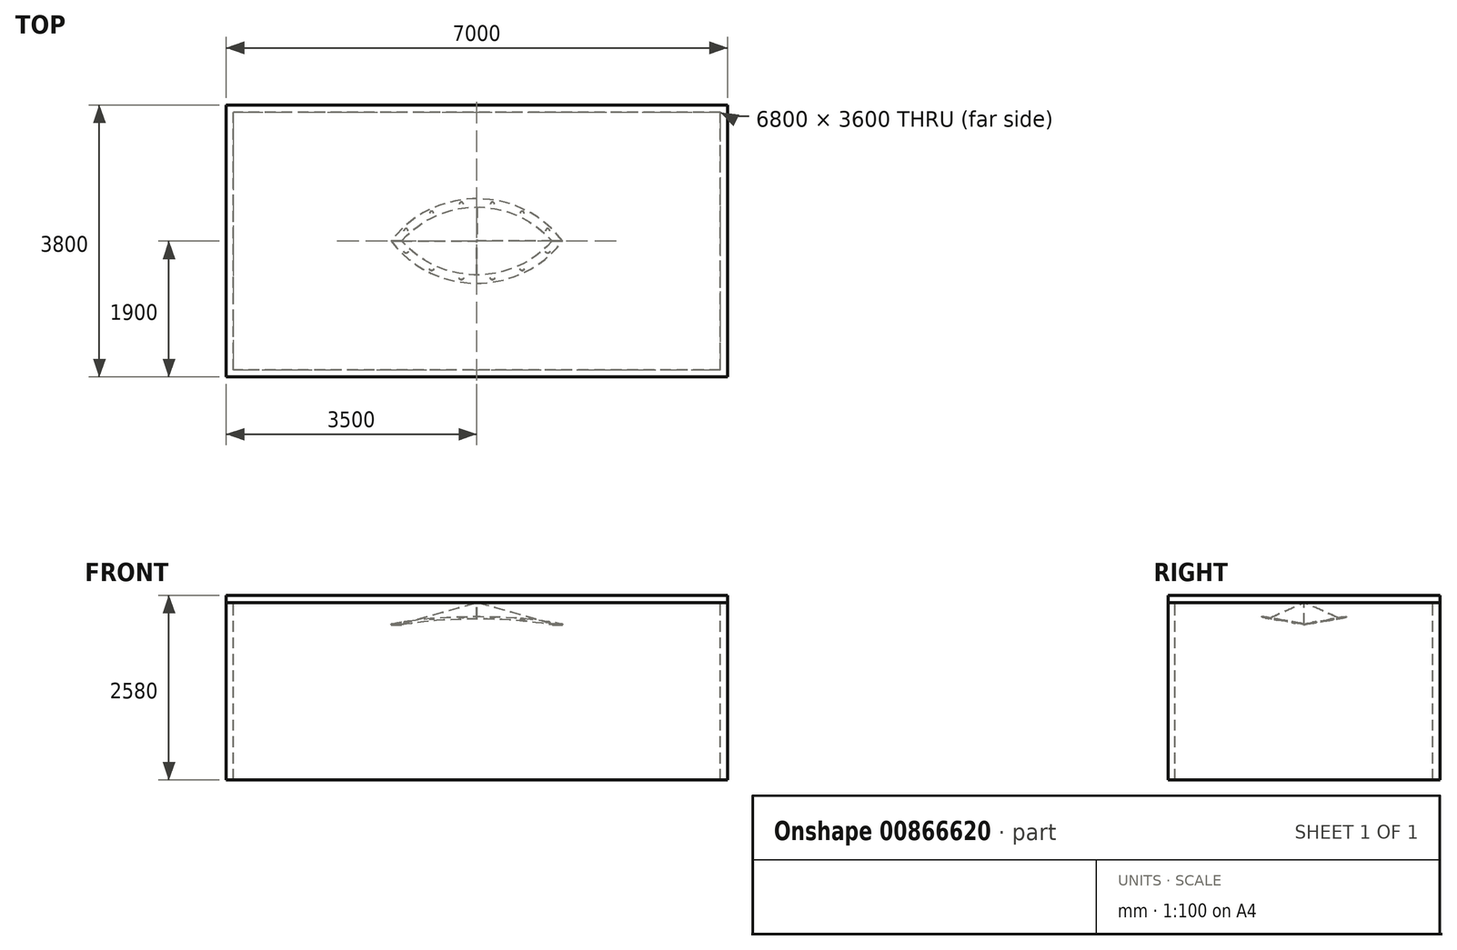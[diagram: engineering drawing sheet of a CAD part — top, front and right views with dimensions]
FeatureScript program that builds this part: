
annotation { "Feature Type Name" : "Feature", "Feature Type Description" : "" }
export const myFeature = defineFeature(function(context is Context, id is Id, definition is map)
    precondition{}
    {
        {
            var Q0;
            Q0=qCreatedBy(makeId("Top.planeOp"),FACE);
            var sketch = newSketch(context, id + "F0", { "sketchPlane" : qUnion([Q0])});
            skLineSegment(sketch, "E0.bottom", {"start": v(0, 0) * mm, "end": v(2400, 0) * mm, "construction": true});
            skLineSegment(sketch, "E0.top", {"start": v(0, 1200) * mm, "end": v(2400, 1200) * mm, "construction": true});
            skLineSegment(sketch, "E0.left", {"start": v(0, 0) * mm, "end": v(0, 1200) * mm, "construction": true});
            skLineSegment(sketch, "E0.right", {"start": v(2400, 0) * mm, "end": v(2400, 1200) * mm, "construction": true});
            skArc(sketch, "E1", {"start": v(2400, 600) * mm, "mid": v(1200, 1200) * mm, "end": v(0, 600) * mm});
            skLineSegment(sketch, "E2", {"start": v(0, 600) * mm, "end": v(2400, 600) * mm});
            skArc(sketch, "E3", {"start": v(2250, 600) * mm, "mid": v(1200, 1082.93) * mm, "end": v(150, 600) * mm});
            skArc(sketch, "E4", {"start": v(75, 600) * mm, "mid": v(1200, 1140.7) * mm, "end": v(2325, 600) * mm, "construction": true});
            skLineSegment(sketch, "E5", {"start": v(2250, 600) * mm, "end": v(2400, 600) * mm, "construction": true});
            skCircle(sketch, "E6", {"center": v(210.48, 747.13) * mm, "radius": 28 * mm});
            skCircle(sketch, "E7.1.0", {"center": v(567.8, 994.59) * mm, "radius": 28 * mm});
            skCircle(sketch, "E7.2.0", {"center": v(982.68, 1124.22) * mm, "radius": 28 * mm});
            skCircle(sketch, "E7.3.0", {"center": v(1417.32, 1124.22) * mm, "radius": 28 * mm});
            skCircle(sketch, "E7.4.0", {"center": v(1832.2, 994.59) * mm, "radius": 28 * mm});
            skCircle(sketch, "E7.5.0", {"center": v(2189.52, 747.13) * mm, "radius": 28 * mm});
            skLineSegment(sketch, "E7.anchor1", {"start": v(1200, -300) * mm, "end": v(210.48, 747.13) * mm, "construction": true});
            skLineSegment(sketch, "E7.anchor2", {"start": v(1200, -300) * mm, "end": v(2189.52, 747.13) * mm, "construction": true});
            skArc(sketch, "E8.MirrorCS", {"start": v(2400, 600) * mm, "mid": v(1200, 0) * mm, "end": v(0, 600) * mm});
            skArc(sketch, "E9.MirrorCS", {"start": v(2250, 600) * mm, "mid": v(1200, 117.07) * mm, "end": v(150, 600) * mm});
            skCircle(sketch, "E10.MirrorC", {"center": v(210.48, 452.87) * mm, "radius": 28 * mm});
            skCircle(sketch, "E11.MirrorC", {"center": v(567.8, 205.41) * mm, "radius": 28 * mm});
            skCircle(sketch, "E12.MirrorC", {"center": v(982.68, 75.78) * mm, "radius": 28 * mm});
            skCircle(sketch, "E13.MirrorC", {"center": v(1417.32, 75.78) * mm, "radius": 28 * mm});
            skCircle(sketch, "E14.MirrorC", {"center": v(1832.2, 205.41) * mm, "radius": 28 * mm});
            skCircle(sketch, "E15.MirrorC", {"center": v(2189.52, 452.87) * mm, "radius": 28 * mm});
            skSolve(sketch);
        }
        {
            var Q0;
            Q0=qCreatedBy(makeId("Right.planeOp"),FACE);
            var sketch = newSketch(context, id + "F1", { "sketchPlane" : qUnion([Q0])});
            skLineSegment(sketch, "E16", {"start": v(600, 0) * mm, "end": v(0, 52.5) * mm, "construction": true});
            skLineSegment(sketch, "E17", {"start": v(600, 0) * mm, "end": v(1200, 52.5) * mm, "construction": true});
            skLineSegment(sketch, "E18", {"start": v(1200, 0) * mm, "end": v(0, 0) * mm, "construction": true});
            skSolve(sketch);
        }
        {
            var Q0;
            Q0=sQuery(id+"F1.wireOp",EDGE,"E17");
            var Q1;
            Q1=sQuery(id+"F0.wireOp",EDGE,"E2");
            cPlane(context, id + "F2", {"entities" : qUnion([Q0, Q1]), "cplaneType" : CPlaneType.LINE_ANGLE, "offset" : 25 * mm, "angle" : 0 * degree, "width" : 150 * mm, "height" : 150 * mm});
        }
        {
            var Q0;
            {var subQ3=sQuery(id+"F0.wireOp",EDGE,"E1");Q0=makeQuery(id+"F0.imprint","IMPRINT",FACE,{"disambiguationData":[TD([[makeQuery(id+"F0.imprint","IMPRINT",EDGE,{"derivedFrom":subQ3}),1.0]])]});}
            extrude(context, id + "F3", {"entities" : qUnion([Q0]), "oppositeDirection" : true, "depth" : 11 * mm});
        }
        {
            var Q0;
            Q0=makeQuery(id+"F3.opExtrude","SWEPT_BODY",BODY,{"disambiguationData":[OSD([sQuery(id+"F0.wireOp",EDGE,"E1"),sQuery(id+"F0.wireOp",EDGE,"E2"),sQuery(id+"F0.wireOp",EDGE,"E3"),sQuery(id+"F0.wireOp",EDGE,"E6"),sQuery(id+"F0.wireOp",EDGE,"E7.1.0"),sQuery(id+"F0.wireOp",EDGE,"E7.2.0"),sQuery(id+"F0.wireOp",EDGE,"E7.3.0"),sQuery(id+"F0.wireOp",EDGE,"E7.4.0"),sQuery(id+"F0.wireOp",EDGE,"E7.5.0")])]});
            var Q1;
            Q1=qCreatedBy(id+"F2.planeOp",FACE);
            mirror(context, id + "F4", {"operationType" : NewBodyOperationType.ADD, "entities" : qUnion([Q0]), "mirrorPlane" : qUnion([Q1])});
        }
        {
            var Q0;
            Q0=makeQuery(id+"F3.opExtrude","SWEPT_BODY",BODY,{"disambiguationData":[OSD([sQuery(id+"F0.wireOp",EDGE,"E1"),sQuery(id+"F0.wireOp",EDGE,"E2"),sQuery(id+"F0.wireOp",EDGE,"E3"),sQuery(id+"F0.wireOp",EDGE,"E6"),sQuery(id+"F0.wireOp",EDGE,"E7.1.0"),sQuery(id+"F0.wireOp",EDGE,"E7.2.0"),sQuery(id+"F0.wireOp",EDGE,"E7.3.0"),sQuery(id+"F0.wireOp",EDGE,"E7.4.0"),sQuery(id+"F0.wireOp",EDGE,"E7.5.0")])]});
            deleteBodies(context, id + "F5", {"entities" : qUnion([Q0])});
        }
        {
            var Q0;
            Q0=qCreatedBy(makeId("Front.planeOp"),FACE);
            cPlane(context, id + "F6", {"entities" : qUnion([Q0]), "cplaneType" : CPlaneType.OFFSET, "offset" : 600 * mm, "oppositeDirection" : true, "width" : 150 * mm, "height" : 150 * mm});
        }
        {
            var Q0;
            Q0=qCreatedBy(makeId("Right.planeOp"),FACE);
            var sketch = newSketch(context, id + "F7", { "sketchPlane" : qUnion([Q0])});
            skLineSegment(sketch, "E19.bottom", {"start": v(600, 11.17) * mm, "end": v(598.09, 11.17) * mm});
            skLineSegment(sketch, "E19.top", {"start": v(600, 0) * mm, "end": v(598.09, 0) * mm});
            skLineSegment(sketch, "E19.left", {"start": v(600, 11.17) * mm, "end": v(600, 0) * mm});
            skLineSegment(sketch, "E19.right", {"start": v(598.09, 11.17) * mm, "end": v(598.09, 0) * mm});
            skSolve(sketch);
        }
        {
            var Q0;
            Q0=makeQuery(id+"F7.imprint","IMPRINT",FACE,{"disambiguationData":[TD([[makeQuery(id+"F7.imprint","IMPRINT",EDGE,{"derivedFrom":sQuery(id+"F7.wireOp",EDGE,"E19.bottom")}),1.0]])]});
            extrude(context, id + "F8", {"entities" : qUnion([Q0]), "operationType" : NewBodyOperationType.REMOVE, "endBound" : BoundingType.THROUGH_ALL, "depth" : 25 * mm});
        }
        {
            var Q0;
            Q0=makeQuery(id+"F4.opPattern","COPY",BODY,{"derivedFrom":makeQuery(id+"F3.opExtrude","SWEPT_BODY",BODY,{"disambiguationData":[OSD([sQuery(id+"F0.wireOp",EDGE,"E1"),sQuery(id+"F0.wireOp",EDGE,"E2"),sQuery(id+"F0.wireOp",EDGE,"E3"),sQuery(id+"F0.wireOp",EDGE,"E6"),sQuery(id+"F0.wireOp",EDGE,"E7.1.0"),sQuery(id+"F0.wireOp",EDGE,"E7.2.0"),sQuery(id+"F0.wireOp",EDGE,"E7.3.0"),sQuery(id+"F0.wireOp",EDGE,"E7.4.0"),sQuery(id+"F0.wireOp",EDGE,"E7.5.0")])]}),"instanceName":"1"});
            var Q1;
            Q1=qCreatedBy(id+"F6.planeOp",FACE);
            mirror(context, id + "F9", {"operationType" : NewBodyOperationType.ADD, "entities" : qUnion([Q0]), "mirrorPlane" : qUnion([Q1])});
        }
        {
            var Q0;
            Q0=makeQuery(id+"F9.opPattern","COPY",EDGE,{"derivedFrom":makeQuery(id+"F4.opPattern","COPY",EDGE,{"derivedFrom":makeQuery(id+"F3.opExtrude","CAP_EDGE",EDGE,{"disambiguationData":[OSD([sQuery(id+"F0.wireOp",EDGE,"E1")])],"isStart":true}),"instanceName":"1"}),"instanceName":"1"});
            var Q1;
            Q1=makeQuery(id+"F9.opPattern","COPY",EDGE,{"derivedFrom":makeQuery(id+"F4.opPattern","COPY",EDGE,{"derivedFrom":makeQuery(id+"F3.opExtrude","CAP_EDGE",EDGE,{"disambiguationData":[OSD([sQuery(id+"F0.wireOp",EDGE,"E1")])],"isStart":false}),"instanceName":"1"}),"instanceName":"1"});
            var Q2;
            Q2=makeQuery(id+"F4.opPattern","COPY",EDGE,{"derivedFrom":makeQuery(id+"F3.opExtrude","CAP_EDGE",EDGE,{"disambiguationData":[OSD([sQuery(id+"F0.wireOp",EDGE,"E1")])],"isStart":false}),"instanceName":"1"});
            var Q3;
            Q3=makeQuery(id+"F4.opPattern","COPY",EDGE,{"derivedFrom":makeQuery(id+"F3.opExtrude","CAP_EDGE",EDGE,{"disambiguationData":[OSD([sQuery(id+"F0.wireOp",EDGE,"E1")])],"isStart":true}),"instanceName":"1"});
            var Q4;
            Q4=makeQuery(id+"F9.opPattern","COPY",EDGE,{"derivedFrom":makeQuery(id+"F4.opPattern","COPY",EDGE,{"derivedFrom":makeQuery(id+"F3.opExtrude","CAP_EDGE",EDGE,{"disambiguationData":[OSD([sQuery(id+"F0.wireOp",EDGE,"E3")])],"isStart":true}),"instanceName":"1"}),"instanceName":"1"});
            var Q5;
            Q5=makeQuery(id+"F4.opPattern","COPY",EDGE,{"derivedFrom":makeQuery(id+"F3.opExtrude","CAP_EDGE",EDGE,{"disambiguationData":[OSD([sQuery(id+"F0.wireOp",EDGE,"E3")])],"isStart":true}),"instanceName":"1"});
            var Q6;
            Q6=makeQuery(id+"F4.opPattern","COPY",EDGE,{"derivedFrom":makeQuery(id+"F3.opExtrude","CAP_EDGE",EDGE,{"disambiguationData":[OSD([sQuery(id+"F0.wireOp",EDGE,"E3")])],"isStart":false}),"instanceName":"1"});
            var Q7;
            Q7=makeQuery(id+"F9.opPattern","COPY",EDGE,{"derivedFrom":makeQuery(id+"F4.opPattern","COPY",EDGE,{"derivedFrom":makeQuery(id+"F3.opExtrude","CAP_EDGE",EDGE,{"disambiguationData":[OSD([sQuery(id+"F0.wireOp",EDGE,"E3")])],"isStart":false}),"instanceName":"1"}),"instanceName":"1"});
            fillet(context, id + "F10", {"entities" : qUnion([Q0, Q1, Q2, Q3, Q4, Q5, Q6, Q7]), "radius" : 3 * mm, "tangentPropagation" : true, "allowEdgeOverflow" : false});
        }
        {
            var Q0;
            Q0=qCreatedBy(id+"F6.planeOp",FACE);
            var sketch = newSketch(context, id + "F11", { "sketchPlane" : qUnion([Q0])});
            skLineSegment(sketch, "E20", {"start": v(1200, 311.17) * mm, "end": v(147.71, 11.17) * mm});
            skLineSegment(sketch, "E21", {"start": v(2252.29, 11.17) * mm, "end": v(1200, 311.17) * mm});
            skCircle(sketch, "E22", {"center": v(1200, 311.17) * mm, "radius": 1 * mm});
            skLineSegment(sketch, "E23", {"start": v(2252.29, 11.17) * mm, "end": v(147.71, 11.17) * mm, "construction": true});
            skSolve(sketch);
        }
        {
            var Q0;
            Q0=sQuery(id+"F11.wireOp",VERTEX,"E21.end");
            var Q1;
            Q1=qCreatedBy(makeId("Right.planeOp"),FACE);
            cPlane(context, id + "F12", {"entities" : qUnion([Q0, Q1]), "cplaneType" : CPlaneType.PLANE_POINT, "offset" : 25 * mm, "width" : 150 * mm, "height" : 150 * mm});
        }
        {
            var Q0;
            Q0=qCreatedBy(id+"F12.planeOp",FACE);
            var sketch = newSketch(context, id + "F13", { "sketchPlane" : qUnion([Q0])});
            skLineSegment(sketch, "E24", {"start": v(600, 311.17) * mm, "end": v(1076.64, 95.21) * mm});
            skLineSegment(sketch, "E25", {"start": v(600, 311.17) * mm, "end": v(123.36, 95.21) * mm});
            skCircle(sketch, "E26", {"center": v(600, 311.17) * mm, "radius": 1 * mm});
            skSolve(sketch);
        }
        {
            var Q0;
            {var subQ0=sQuery(id+"F13.wireOp",EDGE,"E25");var subQ1=sQuery(id+"F13.wireOp",EDGE,"E24");var subQ2=makeQuery(id+"F13.imprint","INTERSECT",VERTEX,{"derivedFrom":[subQ1,subQ0]});Q0=makeQuery(id+"F13.imprint","IMPRINT",FACE,{"disambiguationData":[TD([[makeQuery(id+"F13.imprint","IMPRINT",EDGE,{"disambiguationData":[TD([[subQ2,-1.0]])],"derivedFrom":subQ1}),1.0]])]});}
            var Q1;
            {var subQ0=sQuery(id+"F13.wireOp",EDGE,"E25");var subQ1=sQuery(id+"F13.wireOp",EDGE,"E24");var subQ2=makeQuery(id+"F13.imprint","INTERSECT",VERTEX,{"derivedFrom":[subQ1,subQ0]});Q1=makeQuery(id+"F13.imprint","IMPRINT",FACE,{"disambiguationData":[TD([[makeQuery(id+"F13.imprint","IMPRINT",EDGE,{"disambiguationData":[TD([[subQ2,-1.0]])],"derivedFrom":subQ1}),-1.0]])]});}
            var Q2;
            Q2=sQuery(id+"F11.wireOp",EDGE,"E21");
            sweep(context, id + "F14", {"profiles" : qUnion([Q0, Q1]), "path" : qUnion([Q2])});
        }
        {
            var Q0;
            {var subQ0=sQuery(id+"F13.wireOp",EDGE,"E25");var subQ1=sQuery(id+"F13.wireOp",EDGE,"E24");var subQ2=makeQuery(id+"F13.imprint","INTERSECT",VERTEX,{"derivedFrom":[subQ1,subQ0]});Q0=makeQuery(id+"F13.imprint","IMPRINT",FACE,{"disambiguationData":[TD([[makeQuery(id+"F13.imprint","IMPRINT",EDGE,{"disambiguationData":[TD([[subQ2,-1.0]])],"derivedFrom":subQ1}),1.0]])]});}
            var Q1;
            {var subQ0=sQuery(id+"F13.wireOp",EDGE,"E25");var subQ1=sQuery(id+"F13.wireOp",EDGE,"E24");var subQ2=makeQuery(id+"F13.imprint","INTERSECT",VERTEX,{"derivedFrom":[subQ1,subQ0]});Q1=makeQuery(id+"F13.imprint","IMPRINT",FACE,{"disambiguationData":[TD([[makeQuery(id+"F13.imprint","IMPRINT",EDGE,{"disambiguationData":[TD([[subQ2,-1.0]])],"derivedFrom":subQ1}),-1.0]])]});}
            var Q2;
            Q2=sQuery(id+"F11.wireOp",EDGE,"E20");
            sweep(context, id + "F15", {"profiles" : qUnion([Q0, Q1]), "path" : qUnion([Q2])});
        }
        {
            var Q0;
            {var subQ0=sQuery(id+"F11.wireOp",EDGE,"E21");var subQ1=sQuery(id+"F11.wireOp",EDGE,"E20");var subQ2=makeQuery(id+"F11.imprint","INTERSECT",VERTEX,{"derivedFrom":[subQ1,subQ0]});Q0=makeQuery(id+"F11.imprint","IMPRINT",FACE,{"disambiguationData":[TD([[makeQuery(id+"F11.imprint","IMPRINT",EDGE,{"disambiguationData":[TD([[subQ2,-1.0]])],"derivedFrom":subQ1}),1.0]])]});}
            var Q1;
            {var subQ0=sQuery(id+"F11.wireOp",EDGE,"E21");var subQ1=sQuery(id+"F11.wireOp",EDGE,"E20");var subQ2=makeQuery(id+"F11.imprint","INTERSECT",VERTEX,{"derivedFrom":[subQ1,subQ0]});Q1=makeQuery(id+"F11.imprint","IMPRINT",FACE,{"disambiguationData":[TD([[makeQuery(id+"F11.imprint","IMPRINT",EDGE,{"disambiguationData":[TD([[subQ2,-1.0]])],"derivedFrom":subQ1}),-1.0]])]});}
            var Q2;
            Q2=sQuery(id+"F13.wireOp",EDGE,"E25");
            sweep(context, id + "F16", {"profiles" : qUnion([Q0, Q1]), "path" : qUnion([Q2])});
        }
        {
            var Q0;
            {var subQ0=sQuery(id+"F11.wireOp",EDGE,"E21");var subQ1=sQuery(id+"F11.wireOp",EDGE,"E20");var subQ2=makeQuery(id+"F11.imprint","INTERSECT",VERTEX,{"derivedFrom":[subQ1,subQ0]});Q0=makeQuery(id+"F11.imprint","IMPRINT",FACE,{"disambiguationData":[TD([[makeQuery(id+"F11.imprint","IMPRINT",EDGE,{"disambiguationData":[TD([[subQ2,-1.0]])],"derivedFrom":subQ1}),-1.0]])]});}
            var Q1;
            {var subQ0=sQuery(id+"F11.wireOp",EDGE,"E21");var subQ1=sQuery(id+"F11.wireOp",EDGE,"E20");var subQ2=makeQuery(id+"F11.imprint","INTERSECT",VERTEX,{"derivedFrom":[subQ1,subQ0]});Q1=makeQuery(id+"F11.imprint","IMPRINT",FACE,{"disambiguationData":[TD([[makeQuery(id+"F11.imprint","IMPRINT",EDGE,{"disambiguationData":[TD([[subQ2,-1.0]])],"derivedFrom":subQ1}),1.0]])]});}
            var Q2;
            Q2=sQuery(id+"F13.wireOp",EDGE,"E24");
            sweep(context, id + "F17", {"profiles" : qUnion([Q0, Q1]), "path" : qUnion([Q2])});
        }
        {
            var Q0;
            Q0=sQuery(id+"F13.wireOp",VERTEX,"E26.center");
            var Q1;
            Q1=qCreatedBy(makeId("Top.planeOp"),FACE);
            cPlane(context, id + "F18", {"entities" : qUnion([Q0, Q1]), "cplaneType" : CPlaneType.PLANE_POINT, "offset" : 25 * mm, "width" : 150 * mm, "height" : 150 * mm});
        }
        {
            var Q0;
            Q0=qCreatedBy(id+"F18.planeOp",FACE);
            var sketch = newSketch(context, id + "F19", { "sketchPlane" : qUnion([Q0])});
            skLineSegment(sketch, "E27.bottom", {"start": v(4600, -1201) * mm, "end": v(-2200, -1201) * mm});
            skLineSegment(sketch, "E27.top", {"start": v(4600, 2399) * mm, "end": v(-2200, 2399) * mm});
            skLineSegment(sketch, "E27.left", {"start": v(4600, -1201) * mm, "end": v(4600, 2399) * mm});
            skLineSegment(sketch, "E27.right", {"start": v(-2200, -1201) * mm, "end": v(-2200, 2399) * mm});
            skPoint(sketch, "E27.middle", {"position": v(1200, 599) * mm});
            skLineSegment(sketch, "E28.0", {"start": v(4700, 2499) * mm, "end": v(-2300, 2499) * mm});
            skLineSegment(sketch, "E28.1", {"start": v(4700, -1301) * mm, "end": v(4700, 2499) * mm});
            skLineSegment(sketch, "E28.2", {"start": v(4700, -1301) * mm, "end": v(-2300, -1301) * mm});
            skLineSegment(sketch, "E28.3", {"start": v(-2300, -1301) * mm, "end": v(-2300, 2499) * mm});
            skSolve(sketch);
        }
        {
            var Q0;
            Q0=qSketchRegion(id+"F19",true);
            extrude(context, id + "F20", {"entities" : qUnion([Q0]), "oppositeDirection" : true, "depth" : 2480 * mm});
        }
        {
            var Q0;
            Q0=makeQuery(id+"F19.imprint","IMPRINT",FACE,{"disambiguationData":[TD([[makeQuery(id+"F19.imprint","IMPRINT",EDGE,{"derivedFrom":sQuery(id+"F19.wireOp",EDGE,"E27.bottom")}),-1.0]])]});
            var Q1;
            Q1=makeQuery(id+"F19.imprint","IMPRINT",FACE,{"disambiguationData":[TD([[makeQuery(id+"F19.imprint","IMPRINT",EDGE,{"derivedFrom":sQuery(id+"F19.wireOp",EDGE,"E27.bottom")}),1.0]])]});
            extrude(context, id + "F21", {"entities" : qUnion([Q0, Q1]), "depth" : 100 * mm});
        }
    });
